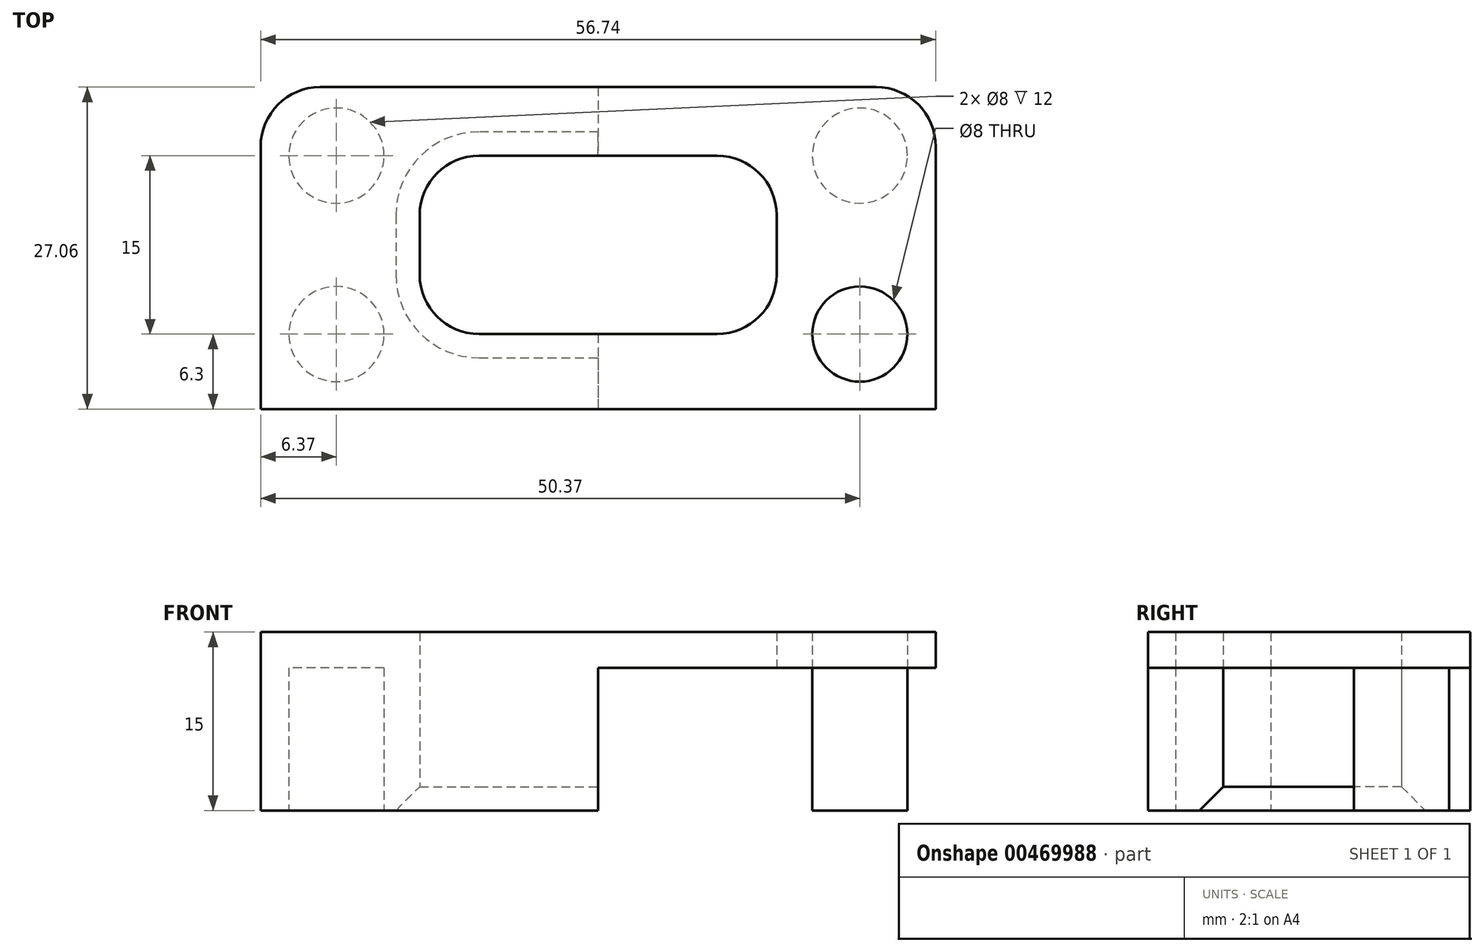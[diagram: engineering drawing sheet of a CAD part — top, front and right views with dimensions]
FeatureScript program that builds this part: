
annotation { "Feature Type Name" : "Feature", "Feature Type Description" : "" }
export const myFeature = defineFeature(function(context is Context, id is Id, definition is map)
    precondition{}
    {
        {
            var Q0;
            Q0=qCreatedBy(makeId("Top.planeOp"),FACE);
            var sketch = newSketch(context, id + "F0", { "sketchPlane" : qUnion([Q0])});
            skLineSegment(sketch, "E0.bottom", {"start": v(0, 0) * mm, "end": v(-30, 0) * mm, "construction": true});
            skLineSegment(sketch, "E0.top", {"start": v(0, 15) * mm, "end": v(-30, 15) * mm, "construction": true});
            skLineSegment(sketch, "E0.left", {"start": v(0, 0) * mm, "end": v(0, 15) * mm, "construction": true});
            skLineSegment(sketch, "E0.right", {"start": v(-30, 0) * mm, "end": v(-30, 15) * mm, "construction": true});
            skLineSegment(sketch, "E1.bottom", {"start": v(0, 15) * mm, "end": v(-22, 15) * mm, "construction": true});
            skLineSegment(sketch, "E1.top", {"start": v(0, 0) * mm, "end": v(-22, 0) * mm, "construction": true});
            skLineSegment(sketch, "E1.left", {"start": v(0, 15) * mm, "end": v(0, 0) * mm, "construction": true});
            skLineSegment(sketch, "E1.right", {"start": v(-22, 15) * mm, "end": v(-22, 0) * mm, "construction": true});
            skCircle(sketch, "E2", {"center": v(-22, 15) * mm, "radius": 4 * mm});
            skCircle(sketch, "E3", {"center": v(-22, 0) * mm, "radius": 4 * mm});
            skLineSegment(sketch, "E4.bottom", {"start": v(0, -6.3) * mm, "end": v(-28.37, -6.3) * mm, "construction": true});
            skLineSegment(sketch, "E4.top", {"start": v(0, 20.76) * mm, "end": v(-28.37, 20.76) * mm, "construction": true});
            skLineSegment(sketch, "E4.left", {"start": v(0, -6.3) * mm, "end": v(0, 20.76) * mm, "construction": true});
            skLineSegment(sketch, "E4.right", {"start": v(-28.37, -6.3) * mm, "end": v(-28.37, 20.76) * mm, "construction": true});
            skLineSegment(sketch, "E5.bottom", {"start": v(0, 20.76) * mm, "end": v(-23.37, 20.76) * mm});
            skLineSegment(sketch, "E5.top", {"start": v(0, -6.3) * mm, "end": v(-28.37, -6.3) * mm});
            skLineSegment(sketch, "E5.left", {"start": v(0, 20.76) * mm, "end": v(0, -6.3) * mm});
            skLineSegment(sketch, "E5.right", {"start": v(-28.37, 15.76) * mm, "end": v(-28.37, -6.3) * mm});
            skCircle(sketch, "E6.MirrorC", {"center": v(22, 15) * mm, "radius": 4 * mm});
            skLineSegment(sketch, "E7.MirrorCS", {"start": v(0, 20.76) * mm, "end": v(23.37, 20.76) * mm});
            skLineSegment(sketch, "E8.MirrorCS", {"start": v(28.37, 15.76) * mm, "end": v(28.37, -6.3) * mm});
            skCircle(sketch, "E9.MirrorC", {"center": v(22, 0) * mm, "radius": 4 * mm});
            skLineSegment(sketch, "E10.MirrorCS", {"start": v(0, -6.3) * mm, "end": v(28.37, -6.3) * mm});
            skLineSegment(sketch, "E11.bottom", {"start": v(0, 0) * mm, "end": v(-10, 0) * mm});
            skLineSegment(sketch, "E11.top", {"start": v(0, 15) * mm, "end": v(-10, 15) * mm});
            skLineSegment(sketch, "E11.left", {"start": v(0, 0) * mm, "end": v(0, 15) * mm});
            skLineSegment(sketch, "E11.right", {"start": v(-15, 5) * mm, "end": v(-15, 10) * mm});
            skPoint(sketch, "E12.visualSharp", {"position": v(-15, 15) * mm});
            skArc(sketch, "E12.filletArc", {"start": v(-10, 15) * mm, "mid": v(-13.54, 13.54) * mm, "end": v(-15, 10) * mm});
            skPoint(sketch, "E13.visualSharp", {"position": v(-15, 0) * mm});
            skArc(sketch, "E13.filletArc", {"start": v(-15, 5) * mm, "mid": v(-13.54, 1.46) * mm, "end": v(-10, 0) * mm});
            skPoint(sketch, "E14.visualSharp", {"position": v(-28.37, 20.76) * mm});
            skArc(sketch, "E14.filletArc", {"start": v(-23.37, 20.76) * mm, "mid": v(-26.9, 19.3) * mm, "end": v(-28.37, 15.76) * mm});
            skPoint(sketch, "E15.visualSharp", {"position": v(28.37, 20.76) * mm});
            skArc(sketch, "E15.filletArc", {"start": v(28.37, 15.76) * mm, "mid": v(26.9, 19.3) * mm, "end": v(23.37, 20.76) * mm});
            skLineSegment(sketch, "E16.MirrorCS", {"start": v(0, 15) * mm, "end": v(10, 15) * mm});
            skArc(sketch, "E17.MirrorCS", {"start": v(10, 15) * mm, "mid": v(13.54, 13.54) * mm, "end": v(15, 10) * mm});
            skLineSegment(sketch, "E18.MirrorCS", {"start": v(15, 5) * mm, "end": v(15, 10) * mm});
            skArc(sketch, "E19.MirrorCS", {"start": v(15, 5) * mm, "mid": v(13.54, 1.46) * mm, "end": v(10, 0) * mm});
            skLineSegment(sketch, "E20.MirrorCS", {"start": v(0, 0) * mm, "end": v(10, 0) * mm});
            skSolve(sketch);
        }
        {
            var Q0;
            Q0=makeQuery(id+"F0.imprint","IMPRINT",FACE,{"disambiguationData":[TD([[makeQuery(id+"F0.imprint","IMPRINT",EDGE,{"derivedFrom":sQuery(id+"F0.wireOp",EDGE,"E2")}),-1.0]])]});
            var Q1;
            Q1=makeQuery(id+"F0.imprint","IMPRINT",FACE,{"disambiguationData":[TD([[makeQuery(id+"F0.imprint","IMPRINT",EDGE,{"derivedFrom":sQuery(id+"F0.wireOp",EDGE,"E6.MirrorC")}),1.0]])]});
            var Q2;
            Q2=makeQuery(id+"F0.imprint","IMPRINT",FACE,{"disambiguationData":[TD([[makeQuery(id+"F0.imprint","IMPRINT",EDGE,{"derivedFrom":sQuery(id+"F0.wireOp",EDGE,"E2")}),1.0]])]});
            var Q3;
            Q3=makeQuery(id+"F0.imprint","IMPRINT",FACE,{"disambiguationData":[TD([[makeQuery(id+"F0.imprint","IMPRINT",EDGE,{"derivedFrom":sQuery(id+"F0.wireOp",EDGE,"E3")}),1.0]])]});
            var Q4;
            Q4=makeQuery(id+"F0.imprint","IMPRINT",FACE,{"disambiguationData":[TD([[makeQuery(id+"F0.imprint","IMPRINT",EDGE,{"derivedFrom":sQuery(id+"F0.wireOp",EDGE,"E6.MirrorC")}),-1.0]])]});
            var Q5;
            Q5=makeQuery(id+"F0.imprint","IMPRINT",FACE,{"disambiguationData":[TD([[makeQuery(id+"F0.imprint","IMPRINT",EDGE,{"derivedFrom":sQuery(id+"F0.wireOp",EDGE,"E9.MirrorC")}),-1.0]])]});
            extrude(context, id + "F1", {"entities" : qUnion([Q0, Q1, Q2, Q3, Q4, Q5]), "depth" : 15 * mm, "offsetDistance" : 25 * mm});
        }
        {
            var Q0;
            Q0=makeQuery(id+"F0.imprint","IMPRINT",FACE,{"disambiguationData":[TD([[makeQuery(id+"F0.imprint","IMPRINT",EDGE,{"derivedFrom":sQuery(id+"F0.wireOp",EDGE,"E6.MirrorC")}),-1.0]])]});
            var Q1;
            Q1=makeQuery(id+"F0.imprint","IMPRINT",FACE,{"disambiguationData":[TD([[makeQuery(id+"F0.imprint","IMPRINT",EDGE,{"derivedFrom":sQuery(id+"F0.wireOp",EDGE,"E9.MirrorC")}),-1.0]])]});
            var Q2;
            Q2=makeQuery(id+"F0.imprint","IMPRINT",FACE,{"disambiguationData":[TD([[makeQuery(id+"F0.imprint","IMPRINT",EDGE,{"derivedFrom":sQuery(id+"F0.wireOp",EDGE,"E2")}),1.0]])]});
            var Q3;
            Q3=makeQuery(id+"F0.imprint","IMPRINT",FACE,{"disambiguationData":[TD([[makeQuery(id+"F0.imprint","IMPRINT",EDGE,{"derivedFrom":sQuery(id+"F0.wireOp",EDGE,"E3")}),1.0]])]});
            extrude(context, id + "F2", {"entities" : qUnion([Q0, Q1, Q2, Q3]), "operationType" : NewBodyOperationType.REMOVE, "depth" : 12 * mm, "offsetDistance" : 25 * mm});
        }
        {
            var Q0;
            Q0=makeQuery(id+"F1.opExtrude","CAP_EDGE",EDGE,{"disambiguationData":[OSD([sQuery(id+"F0.wireOp",EDGE,"E11.top"),sQuery(id+"F0.wireOp",EDGE,"E16.MirrorCS")])],"isStart":true});
            chamfer(context, id + "F3", {"entities" : qUnion([Q0]), "width" : 2 * mm, "tangentPropagation" : true});
        }
    });
